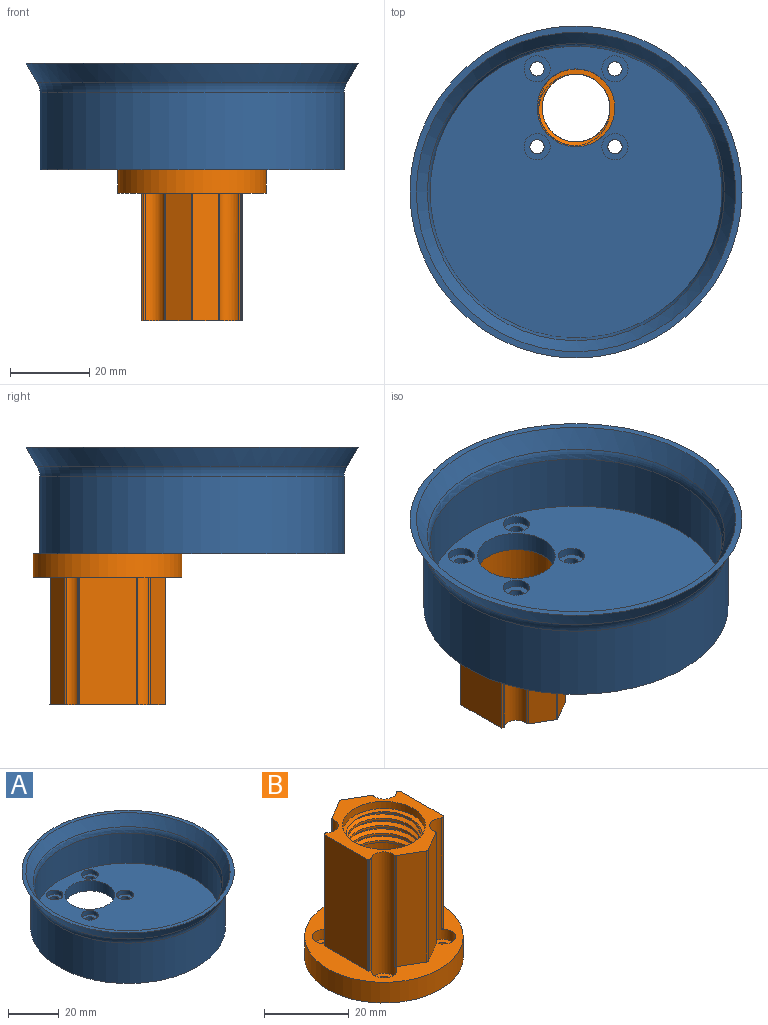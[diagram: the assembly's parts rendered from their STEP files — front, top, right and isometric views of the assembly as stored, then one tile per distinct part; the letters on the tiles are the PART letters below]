
ASSEMBLY  parts=2 mates=1
PART A: 22 faces, bbox 86.4x86.4x26.9 mm
  f0: cylinder r=1.8mm len=3.6mm, axis (0,0,1), area 33.9mm2, adj f7,f16
  f1: cylinder r=1.8mm len=3.6mm, axis (0,0,1), area 33.9mm2, adj f7,f14
  f2: cylinder r=1.8mm len=3.6mm, axis (0,0,1), area 33.9mm2, adj f7,f12
  f3: cylinder r=1.8mm len=3.6mm, axis (0,0,1), area 33.9mm2, adj f7,f10
  f4: plane 73.66x73.66mm, normal (0,0,1), area 3821.3mm2, adj f6,f8,f9,f11,f13,f15
  f5: cylinder r=38.43mm len=76.86mm, axis (0,0,1), area 4711.9mm2, adj f7,f21
  f6: cylinder r=9.83mm len=19.65mm, axis (0,0,1), area 308.7mm2, adj f4,f7
  f7: plane 76.86x76.86mm, normal (0,0,-1), area 4295.7mm2, adj f0,f1,f2,f3,f5,f6
  f8: cylinder r=36.83mm len=73.66mm, axis (0,0,-1), area 3358.6mm2, adj f4,f20
  f9: cylinder r=3.3mm len=6.6mm, axis (0,0,1), area 41.5mm2, adj f4,f10
  f10: plane 6.6x6.6mm, normal (0,0,1), area 24mm2, adj f3,f9
  f11: cylinder r=3.3mm len=6.6mm, axis (0,0,1), area 41.5mm2, adj f4,f12
  f12: plane 6.6x6.6mm, normal (0,0,1), area 24mm2, adj f2,f11
  f13: cylinder r=3.3mm len=6.6mm, axis (0,0,1), area 41.5mm2, adj f4,f14
  f14: plane 6.6x6.6mm, normal (0,0,1), area 24mm2, adj f1,f13
  f15: cylinder r=3.3mm len=6.6mm, axis (0,0,1), area 41.5mm2, adj f4,f16
  f16: plane 6.6x6.6mm, normal (0,0,1), area 24mm2, adj f0,f15
  f17: cone r=40.29mm half-angle=30deg, axis (0,0,1), area 1360.8mm2, adj f19,f20
  f18: cone r=38.43mm half-angle=30deg, axis (0,0,1), area 1416.7mm2, adj f19,f21
  f19: plane 83.79x83.79mm, normal (0,0,1), area 413.1mm2, adj f17,f18
  f20: torus R=41.91mm, axis (0,0,1), area 619.3mm2, adj f8,f17
  f21: torus R=43.51mm, axis (0,0,1), area 646.1mm2, adj f5,f18
PART B: 47 faces, bbox 38x38x38.7 mm
  f0: cylinder r=3.07mm len=35.22mm, axis (0,0,-1), area 304.1mm2, adj f21,f25,f33,f34,f35
  f1: cylinder r=3.07mm len=35.22mm, axis (0,0,-1), area 304.1mm2, adj f21,f25,f31,f36,f37
  f2: cylinder r=3.07mm len=35.22mm, axis (0,0,-1), area 304.1mm2, adj f21,f25,f29,f38,f39
  f3: cylinder r=3.07mm len=35.22mm, axis (0,0,-1), area 304.1mm2, adj f21,f25,f27,f40,f41
  f4: plane 32.22x0.19mm, normal (0.5,0.87,0), area 7mm2, adj f21,f25,f37,f42
  f5: plane 32.22x6.42mm, normal (-0.5,0.87,0), area 238.7mm2, adj f21,f25,f35,f43
  f6: plane 32.22x0.19mm, normal (-0.5,-0.87,0), area 7mm2, adj f21,f25,f41,f44
  f7: plane 32.22x6.42mm, normal (0.5,-0.87,0), area 238.7mm2, adj f21,f25,f38,f45
  f8: plane 32.22x14.2mm, normal (1,0,0), area 457.6mm2, adj f21,f25,f42,f46
  f9: plane 32.22x6.42mm, normal (0.5,0.87,0), area 238.7mm2, adj f21,f25,f36,f43
  f10: plane 32.22x0.39mm, normal (-0.5,0.87,0), area 14.4mm2, adj f11,f21,f25,f34
  f11: plane 32.22x14.43mm, normal (-1,0,0), area 465mm2, adj f10,f21,f25,f44
  f12: plane 32.22x6.42mm, normal (-0.5,-0.87,0), area 238.7mm2, adj f21,f25,f40,f45
  f13: plane 32.22x0.19mm, normal (0.5,-0.87,0), area 7mm2, adj f21,f25,f39,f46
  f14: plane 20.09x20.09mm, normal (0,0,-1), area 48.3mm2, adj f15,f16,f17,f18,f22
  f15: cylinder r=8.55mm len=17.11mm, axis (0,0,1), area 139.7mm2, adj f14,f16,f18,f19
  f16: bspline ~21.95x19.01mm, area 266.4mm2, adj f14,f15,f17,f19
  f17: cylinder r=9.51mm len=19.01mm, axis (0,0,1), area 117.3mm2, adj f14,f16,f18,f19
  f18: bspline ~21.95x19.01mm, area 266.5mm2, adj f14,f15,f17,f19
  f19: plane 20.12x20.12mm, normal (0,0,1), area 48.4mm2, adj f15,f16,f17,f18,f20
  f20: cylinder r=9.83mm len=19.65mm, axis (0,0,1), area 127.1mm2, adj f19,f21
  f21: plane 29.21x25.4mm, normal (0,0,1), area 213.5mm2, adj f0,f1,f2,f3,f4,f5,f6,f7
  f22: cylinder r=9.83mm len=26.92mm, axis (0,0,1), area 1662.1mm2, adj f14,f23
  f23: plane 37.54x37.54mm, normal (0,0,-1), area 762.8mm2, adj f22,f24,f26,f28,f30,f32
  f24: cylinder r=18.77mm len=37.54mm, axis (0,0,-1), area 707.6mm2, adj f23,f25
  f25: plane 37.54x37.54mm, normal (0,0,1), area 471.2mm2, adj f0,f1,f2,f3,f4,f5,f6,f7
  f26: cylinder r=1.8mm len=3.6mm, axis (0,0,-1), area 33.9mm2, adj f23,f27
  f27: plane 6.15x6.15mm, normal (0,0,1), area 19.5mm2, adj f3,f26
  f28: cylinder r=1.8mm len=3.6mm, axis (0,0,-1), area 33.9mm2, adj f23,f29
  f29: plane 6.15x6.15mm, normal (0,0,1), area 19.5mm2, adj f2,f28
  f30: cylinder r=1.8mm len=3.6mm, axis (0,0,-1), area 33.9mm2, adj f23,f31
  f31: plane 6.15x6.15mm, normal (0,0,1), area 19.5mm2, adj f1,f30
  f32: cylinder r=1.8mm len=3.6mm, axis (0,0,-1), area 33.9mm2, adj f23,f33
  f33: plane 6.15x6.15mm, normal (0,0,1), area 19.5mm2, adj f0,f32
  f34: cylinder r=0.4mm len=32.22mm, axis (0,0,-1), area 16mm2, adj f0,f10,f21,f25
  f35: cylinder r=0.4mm len=32.22mm, axis (0,0,-1), area 16mm2, adj f0,f5,f21,f25
  f36: cylinder r=0.4mm len=32.22mm, axis (0,0,-1), area 16mm2, adj f1,f9,f21,f25
  f37: cylinder r=0.4mm len=32.22mm, axis (0,0,-1), area 16mm2, adj f1,f4,f21,f25
  f38: cylinder r=0.4mm len=32.22mm, axis (0,0,-1), area 16mm2, adj f2,f7,f21,f25
  f39: cylinder r=0.4mm len=32.22mm, axis (0,0,-1), area 16mm2, adj f2,f13,f21,f25
  f40: cylinder r=0.4mm len=32.22mm, axis (0,0,-1), area 16mm2, adj f3,f12,f21,f25
  f41: cylinder r=0.4mm len=32.22mm, axis (0,0,-1), area 16mm2, adj f3,f6,f21,f25
  f42: cylinder r=0.4mm len=32.22mm, axis (0,0,1), area 13.5mm2, adj f4,f8,f21,f25
  f43: cylinder r=0.4mm len=32.22mm, axis (0,0,1), area 13.5mm2, adj f5,f9,f21,f25
  f44: cylinder r=0.4mm len=32.22mm, axis (0,0,1), area 13.5mm2, adj f6,f11,f21,f25
  f45: cylinder r=0.4mm len=32.22mm, axis (0,0,1), area 13.5mm2, adj f7,f12,f21,f25
  f46: cylinder r=0.4mm len=32.22mm, axis (0,0,1), area 13.5mm2, adj f8,f13,f21,f25
PLACE A t=(0,0,6.35)mm fixed
PLACE B rot(axis=(1,0,0),180deg) t=(0,21.29,-36.37)mm
MATE fastened B.f2 <-> A.f0  axis (0,0,1) through (9.83,31.11,1.35)mm
